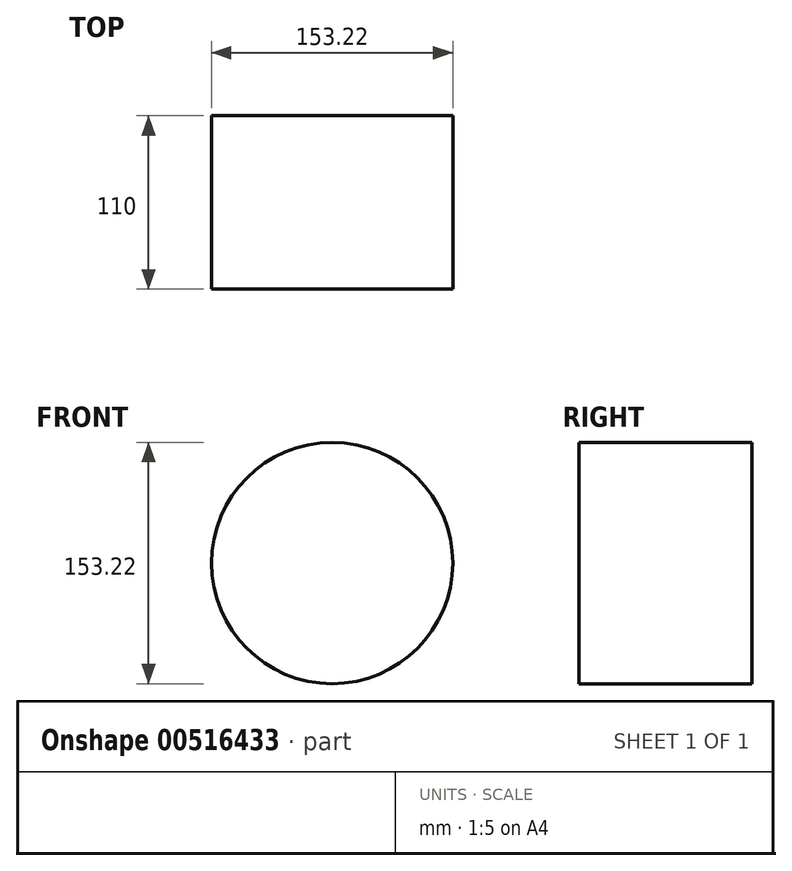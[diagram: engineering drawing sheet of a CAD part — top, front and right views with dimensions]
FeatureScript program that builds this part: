
annotation { "Feature Type Name" : "Feature", "Feature Type Description" : "" }
export const myFeature = defineFeature(function(context is Context, id is Id, definition is map)
    precondition{}
    {
        {
            var Q0;
            Q0=qCreatedBy(makeId("Front.planeOp"),FACE);
            var sketch = newSketch(context, id + "F0", { "sketchPlane" : qUnion([Q0])});
            skCircle(sketch, "E0", {"center": v(0, 0) * mm, "radius": 76.61 * mm});
            skSolve(sketch);
        }
        {
            var Q0;
            Q0=makeQuery(id+"F0.imprint","IMPRINT",FACE,{"disambiguationData":[TD([[makeQuery(id+"F0.imprint","IMPRINT",EDGE,{"derivedFrom":sQuery(id+"F0.wireOp",EDGE,"E0")}),1.0]])]});
            extrude(context, id + "F1", {"entities" : qUnion([Q0]), "depth" : 110 * mm, "offsetDistance" : 25.4 * mm});
        }
    });
